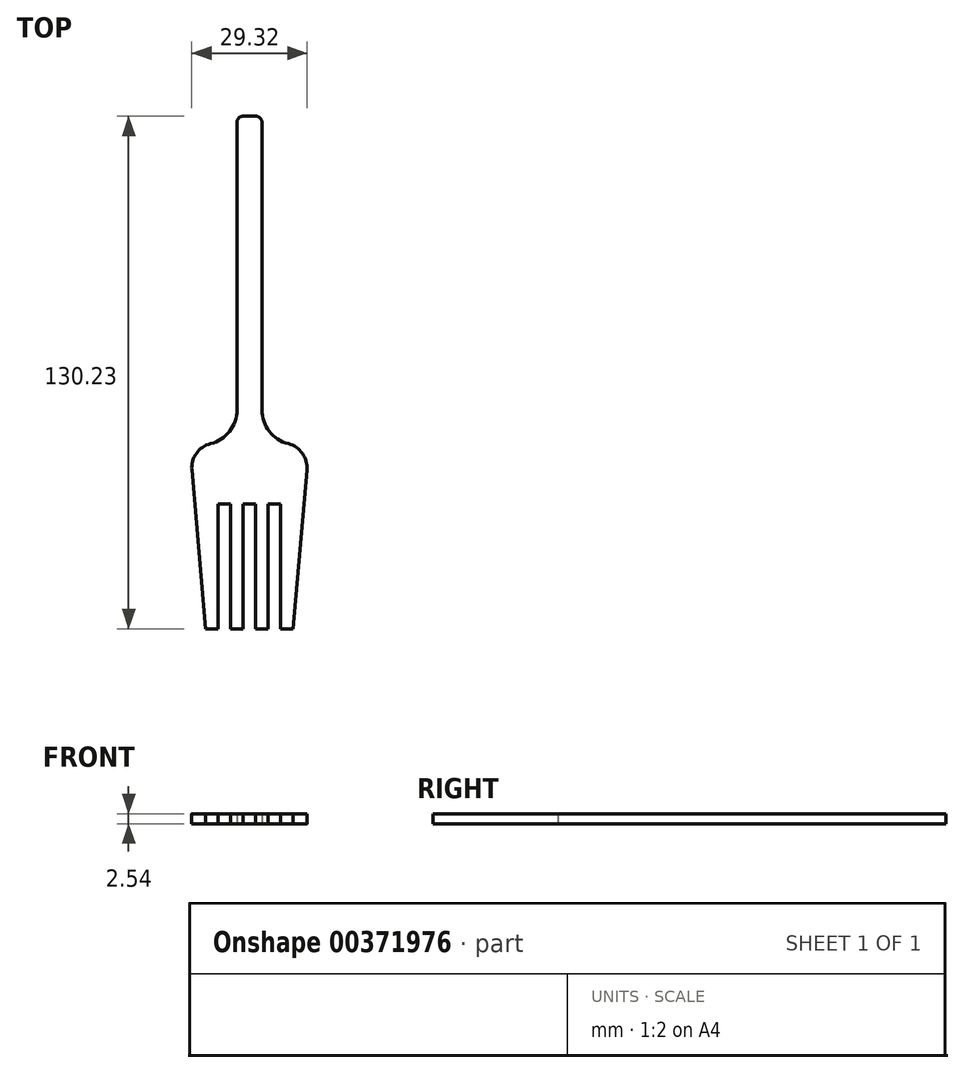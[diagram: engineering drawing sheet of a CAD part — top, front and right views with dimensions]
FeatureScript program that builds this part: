
annotation { "Feature Type Name" : "Feature", "Feature Type Description" : "" }
export const myFeature = defineFeature(function(context is Context, id is Id, definition is map)
    precondition{}
    {
        {
            var Q0;
            Q0=qCreatedBy(makeId("Top.planeOp"),FACE);
            var sketch = newSketch(context, id + "F0", { "sketchPlane" : qUnion([Q0])});
            skLineSegment(sketch, "E0.bottom", {"start": v(-1.59, 74.61) * mm, "end": v(1.59, 74.61) * mm});
            skLineSegment(sketch, "E0.left", {"start": v(-3.17, 73.02) * mm, "end": v(-3.18, 0) * mm});
            skLineSegment(sketch, "E0.right", {"start": v(3.17, 73.02) * mm, "end": v(3.18, 0) * mm});
            skLineSegment(sketch, "E1", {"start": v(0, 0) * mm, "end": v(0, 52.08) * mm, "construction": true});
            skPoint(sketch, "E2.visualSharp", {"position": v(-3.17, 74.61) * mm});
            skArc(sketch, "E2.filletArc", {"start": v(-1.59, 74.61) * mm, "mid": v(-2.71, 74.15) * mm, "end": v(-3.17, 73.02) * mm});
            skPoint(sketch, "E3.visualSharp", {"position": v(3.17, 74.61) * mm});
            skArc(sketch, "E3.filletArc", {"start": v(3.17, 73.02) * mm, "mid": v(2.71, 74.15) * mm, "end": v(1.59, 74.61) * mm});
            skLineSegment(sketch, "E4", {"start": v(-7.94, -55.62) * mm, "end": v(-7.94, -23.87) * mm});
            skLineSegment(sketch, "E5", {"start": v(-1.59, -55.62) * mm, "end": v(-1.59, -23.87) * mm});
            skLineSegment(sketch, "E6", {"start": v(-4.76, -55.62) * mm, "end": v(-4.76, -23.87) * mm});
            skLineSegment(sketch, "E7", {"start": v(7.94, -55.62) * mm, "end": v(7.94, -23.87) * mm});
            skLineSegment(sketch, "E8", {"start": v(1.59, -55.62) * mm, "end": v(1.59, -23.87) * mm});
            skLineSegment(sketch, "E9", {"start": v(4.76, -55.62) * mm, "end": v(4.76, -23.87) * mm});
            skArc(sketch, "E10", {"start": v(-3.18, 0) * mm, "mid": v(-5.05, -5.46) * mm, "end": v(-9.88, -8.62) * mm});
            skArc(sketch, "E11", {"start": v(-9.88, -8.62) * mm, "mid": v(-13.5, -11.1) * mm, "end": v(-14.64, -15.32) * mm});
            skLineSegment(sketch, "E12", {"start": v(-7.94, -55.62) * mm, "end": v(-11.11, -55.62) * mm});
            skLineSegment(sketch, "E13", {"start": v(-11.11, -55.62) * mm, "end": v(-14.64, -15.32) * mm});
            skLineSegment(sketch, "E14", {"start": v(-7.94, -23.87) * mm, "end": v(-4.76, -23.87) * mm});
            skLineSegment(sketch, "E15", {"start": v(-4.76, -55.62) * mm, "end": v(-1.59, -55.62) * mm});
            skLineSegment(sketch, "E16", {"start": v(-1.59, -23.87) * mm, "end": v(1.59, -23.87) * mm});
            skLineSegment(sketch, "E17", {"start": v(1.59, -55.62) * mm, "end": v(4.76, -55.62) * mm});
            skLineSegment(sketch, "E18", {"start": v(4.76, -23.87) * mm, "end": v(7.94, -23.87) * mm});
            skLineSegment(sketch, "E19", {"start": v(7.94, -55.62) * mm, "end": v(11.11, -55.62) * mm});
            skArc(sketch, "E20", {"start": v(3.18, 0) * mm, "mid": v(5.05, -5.46) * mm, "end": v(9.88, -8.62) * mm});
            skLineSegment(sketch, "E21", {"start": v(11.11, -55.62) * mm, "end": v(14.64, -15.32) * mm});
            skArc(sketch, "E22", {"start": v(9.88, -8.62) * mm, "mid": v(13.5, -11.1) * mm, "end": v(14.64, -15.32) * mm});
            skSolve(sketch);
        }
        {
            var Q0;
            Q0=makeQuery(id+"F0.imprint","IMPRINT",FACE,{"disambiguationData":[TD([[makeQuery(id+"F0.imprint","IMPRINT",EDGE,{"derivedFrom":sQuery(id+"F0.wireOp",EDGE,"E0.bottom")}),-1.0]])]});
            extrude(context, id + "F1", {"entities" : qUnion([Q0]), "depth" : 2.54 * mm});
        }
    });
